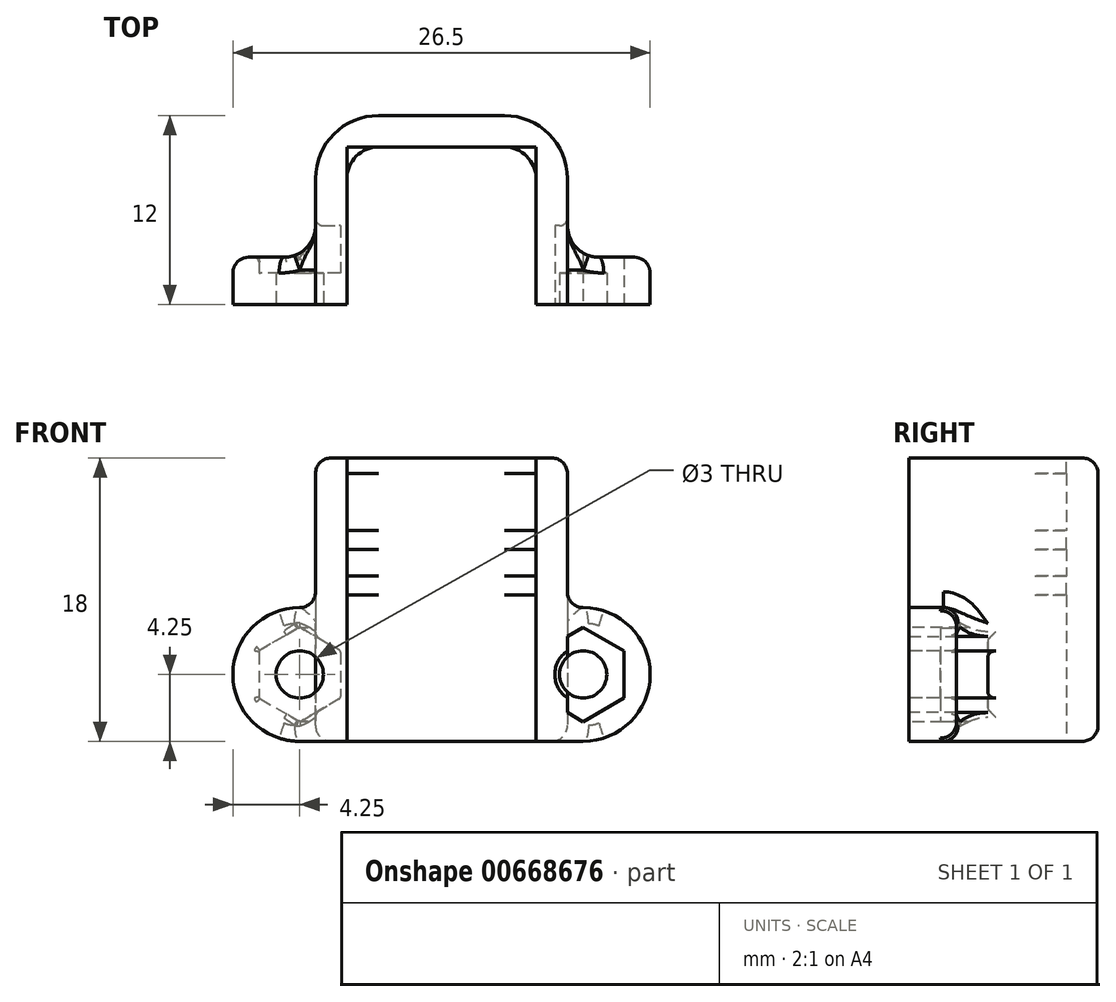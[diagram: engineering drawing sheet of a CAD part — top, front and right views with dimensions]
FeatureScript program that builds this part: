
annotation { "Feature Type Name" : "Feature", "Feature Type Description" : "" }
export const myFeature = defineFeature(function(context is Context, id is Id, definition is map)
    precondition{}
    {
        {
            var Q0;
            Q0=qCreatedBy(makeId("Top.planeOp"),FACE);
            var sketch = newSketch(context, id + "F0", { "sketchPlane" : qUnion([Q0])});
            skLineSegment(sketch, "E0", {"start": v(0, 0) * mm, "end": v(0, 8) * mm});
            skLineSegment(sketch, "E1", {"start": v(2, 10) * mm, "end": v(10, 10) * mm});
            skLineSegment(sketch, "E2", {"start": v(12, 8) * mm, "end": v(12, 0) * mm});
            skLineSegment(sketch, "E3", {"start": v(12, 0) * mm, "end": v(0, 0) * mm, "construction": true});
            skPoint(sketch, "E4.visualSharp", {"position": v(0, 10) * mm});
            skArc(sketch, "E4.filletArc", {"start": v(2, 10) * mm, "mid": v(0.59, 9.41) * mm, "end": v(0, 8) * mm});
            skPoint(sketch, "E5.visualSharp", {"position": v(12, 10) * mm});
            skArc(sketch, "E5.filletArc", {"start": v(12, 8) * mm, "mid": v(11.41, 9.41) * mm, "end": v(10, 10) * mm});
            skLineSegment(sketch, "E6.0", {"start": v(-2, 0) * mm, "end": v(-2, 8) * mm});
            skLineSegment(sketch, "E6.1", {"start": v(14, 8) * mm, "end": v(14, 0) * mm});
            skArc(sketch, "E6.2", {"start": v(14, 8) * mm, "mid": v(12.83, 10.83) * mm, "end": v(10, 12) * mm});
            skLineSegment(sketch, "E6.3", {"start": v(2, 12) * mm, "end": v(10, 12) * mm});
            skArc(sketch, "E6.4", {"start": v(2, 12) * mm, "mid": v(-0.83, 10.83) * mm, "end": v(-2, 8) * mm});
            skLineSegment(sketch, "E7", {"start": v(-2, 0) * mm, "end": v(0, 0) * mm});
            skLineSegment(sketch, "E8", {"start": v(12, 0) * mm, "end": v(14, 0) * mm});
            skSolve(sketch);
        }
        {
            var Q0;
            Q0=qSketchRegion(id+"F0",true);
            extrude(context, id + "F1", {"entities" : qUnion([Q0]), "depth" : 18 * mm});
        }
        {
            var Q0;
            Q0=qCreatedBy(makeId("Front.planeOp"),FACE);
            var sketch = newSketch(context, id + "F2", { "sketchPlane" : qUnion([Q0])});
            skCircle(sketch, "E9", {"center": v(-3, 4.25) * mm, "radius": 1.8 * mm});
            skCircle(sketch, "E10", {"center": v(-3, 4.25) * mm, "radius": 1.5 * mm});
            skLineSegment(sketch, "E11.bottom", {"start": v(1.25, 8.5) * mm, "end": v(-3, 8.5) * mm, "construction": true});
            skLineSegment(sketch, "E11.top", {"start": v(1.25, 0) * mm, "end": v(-3, 0) * mm, "construction": true});
            skLineSegment(sketch, "E11.left", {"start": v(1.25, 8.5) * mm, "end": v(1.25, 0) * mm, "construction": true});
            skLineSegment(sketch, "E11.right", {"start": v(-7.25, 8.5) * mm, "end": v(-7.25, 0) * mm, "construction": true});
            skLineSegment(sketch, "E12", {"start": v(6, 0) * mm, "end": v(6, 18.17) * mm, "construction": true});
            skLineSegment(sketch, "E13", {"start": v(-3, 0) * mm, "end": v(-7.25, 0) * mm, "construction": true});
            skLineSegment(sketch, "E14", {"start": v(-3, 8.5) * mm, "end": v(-7.25, 8.5) * mm, "construction": true});
            skArc(sketch, "E15", {"start": v(-3, 8.5) * mm, "mid": v(-7.25, 4.25) * mm, "end": v(-3, 0) * mm});
            skArc(sketch, "E16", {"start": v(-3, 0) * mm, "mid": v(1.25, 4.25) * mm, "end": v(-3, 8.5) * mm, "construction": true});
            skLineSegment(sketch, "E17", {"start": v(-3, 0) * mm, "end": v(0, 0) * mm});
            skLineSegment(sketch, "E18", {"start": v(0, 0) * mm, "end": v(0, 8.5) * mm});
            skLineSegment(sketch, "E19", {"start": v(0, 8.5) * mm, "end": v(-3, 8.5) * mm});
            skLineSegment(sketch, "E20.MirrorCS", {"start": v(15, 0) * mm, "end": v(12, 0) * mm});
            skLineSegment(sketch, "E21.MirrorCS", {"start": v(12, 8.5) * mm, "end": v(15, 8.5) * mm});
            skCircle(sketch, "E22.MirrorC", {"center": v(15, 4.25) * mm, "radius": 1.5 * mm});
            skCircle(sketch, "E23.MirrorC", {"center": v(15, 4.25) * mm, "radius": 1.8 * mm});
            skLineSegment(sketch, "E24.MirrorCS", {"start": v(10.75, 8.5) * mm, "end": v(10.75, 0) * mm, "construction": true});
            skLineSegment(sketch, "E25.MirrorCS", {"start": v(15, 8.5) * mm, "end": v(19.25, 8.5) * mm, "construction": true});
            skLineSegment(sketch, "E26.MirrorCS", {"start": v(10.75, 0) * mm, "end": v(15, 0) * mm, "construction": true});
            skArc(sketch, "E27.MirrorCS", {"start": v(15, 0) * mm, "mid": v(10.75, 4.25) * mm, "end": v(15, 8.5) * mm, "construction": true});
            skLineSegment(sketch, "E28.MirrorCS", {"start": v(10.75, 8.5) * mm, "end": v(15, 8.5) * mm, "construction": true});
            skLineSegment(sketch, "E29.MirrorCS", {"start": v(19.25, 8.5) * mm, "end": v(19.25, 0) * mm, "construction": true});
            skLineSegment(sketch, "E30.MirrorCS", {"start": v(15, 0) * mm, "end": v(19.25, 0) * mm, "construction": true});
            skLineSegment(sketch, "E31.MirrorCS", {"start": v(12, 0) * mm, "end": v(12, 8.5) * mm});
            skArc(sketch, "E32.MirrorCS", {"start": v(15, 8.5) * mm, "mid": v(19.25, 4.25) * mm, "end": v(15, 0) * mm});
            skCircle(sketch, "E33", {"center": v(15, 4.25) * mm, "radius": 3 * mm, "construction": true});
            skLineSegment(sketch, "E34.0", {"start": v(17.6, 5.75) * mm, "end": v(17.6, 2.75) * mm});
            skLineSegment(sketch, "E34.1", {"start": v(17.6, 2.75) * mm, "end": v(15, 1.25) * mm});
            skLineSegment(sketch, "E34.2", {"start": v(15, 1.25) * mm, "end": v(12.4, 2.75) * mm});
            skLineSegment(sketch, "E34.3", {"start": v(12.4, 2.75) * mm, "end": v(12.4, 5.75) * mm});
            skLineSegment(sketch, "E34.4", {"start": v(12.4, 5.75) * mm, "end": v(15, 7.25) * mm});
            skLineSegment(sketch, "E34.5", {"start": v(15, 7.25) * mm, "end": v(17.6, 5.75) * mm});
            skLineSegment(sketch, "E35.MirrorCS", {"start": v(-5.6, 5.75) * mm, "end": v(-5.6, 2.75) * mm});
            skLineSegment(sketch, "E36.MirrorCS", {"start": v(-3, 7.25) * mm, "end": v(-5.6, 5.75) * mm});
            skLineSegment(sketch, "E37.MirrorCS", {"start": v(-0.4, 5.75) * mm, "end": v(-3, 7.25) * mm});
            skLineSegment(sketch, "E38.MirrorCS", {"start": v(-0.4, 2.75) * mm, "end": v(-0.4, 5.75) * mm});
            skLineSegment(sketch, "E39.MirrorCS", {"start": v(-3, 1.25) * mm, "end": v(-0.4, 2.75) * mm});
            skLineSegment(sketch, "E40.MirrorCS", {"start": v(-5.6, 2.75) * mm, "end": v(-3, 1.25) * mm});
            skSolve(sketch);
        }
        {
            var Q0;
            Q0=makeQuery(id+"F2.imprint","IMPRINT",FACE,{"disambiguationData":[TD([[makeQuery(id+"F2.imprint","IMPRINT",EDGE,{"derivedFrom":sQuery(id+"F2.wireOp",EDGE,"E9")}),-1.0]])]});
            var Q1;
            Q1=makeQuery(id+"F2.imprint","IMPRINT",FACE,{"disambiguationData":[TD([[makeQuery(id+"F2.imprint","IMPRINT",EDGE,{"derivedFrom":sQuery(id+"F2.wireOp",EDGE,"E9")}),1.0]])]});
            var Q2;
            Q2=makeQuery(id+"F2.imprint","IMPRINT",FACE,{"disambiguationData":[TD([[makeQuery(id+"F2.imprint","IMPRINT",EDGE,{"derivedFrom":sQuery(id+"F2.wireOp",EDGE,"E20.MirrorCS")}),-1.0]])]});
            var Q3;
            Q3=makeQuery(id+"F2.imprint","IMPRINT",FACE,{"disambiguationData":[TD([[makeQuery(id+"F2.imprint","IMPRINT",EDGE,{"derivedFrom":sQuery(id+"F2.wireOp",EDGE,"E22.MirrorC")}),1.0]])]});
            var Q4;
            Q4=makeQuery(id+"F2.imprint","IMPRINT",FACE,{"disambiguationData":[TD([[makeQuery(id+"F2.imprint","IMPRINT",EDGE,{"derivedFrom":sQuery(id+"F2.wireOp",EDGE,"E23.MirrorC")}),1.0]])]});
            var Q5;
            Q5=makeQuery(id+"F2.imprint","IMPRINT",FACE,{"disambiguationData":[TD([[makeQuery(id+"F2.imprint","IMPRINT",EDGE,{"derivedFrom":sQuery(id+"F2.wireOp",EDGE,"E15")}),1.0]])]});
            extrude(context, id + "F3", {"entities" : qUnion([Q0, Q1, Q2, Q3, Q4, Q5]), "operationType" : NewBodyOperationType.ADD, "oppositeDirection" : true, "depth" : 3 * mm});
        }
        {
            var Q0;
            Q0=makeQuery(id+"F2.imprint","IMPRINT",FACE,{"disambiguationData":[TD([[makeQuery(id+"F2.imprint","IMPRINT",EDGE,{"derivedFrom":sQuery(id+"F2.wireOp",EDGE,"E10")}),1.0]])]});
            var Q1;
            Q1=makeQuery(id+"F2.imprint","IMPRINT",FACE,{"disambiguationData":[TD([[makeQuery(id+"F2.imprint","IMPRINT",EDGE,{"derivedFrom":sQuery(id+"F2.wireOp",EDGE,"E22.MirrorC")}),-1.0]])]});
            var Q2;
            Q2=sQuery(id+"F2.wireOp",EDGE,"E10");
            extrude(context, id + "F4", {"entities" : qUnion([Q0, Q1]), "operationType" : NewBodyOperationType.REMOVE, "surfaceEntities" : qUnion([Q2]), "oppositeDirection" : true, "depth" : 5 * mm});
        }
        {
            var Q0;
            Q0=makeQuery(id+"F3.boolean.opBoolean","INTERSECT",EDGE,{"derivedFrom":[makeQuery(id+"F1.opExtrude","SWEPT_FACE",FACE,{"disambiguationData":[OSD([sQuery(id+"F0.wireOp",EDGE,"E6.1")])]}),makeQuery(id+"F3.opExtrude","CAP_FACE",FACE,{"disambiguationData":[OSD([sQuery(id+"F2.wireOp",EDGE,"E20.MirrorCS"),sQuery(id+"F2.wireOp",EDGE,"E21.MirrorCS"),sQuery(id+"F2.wireOp",EDGE,"E22.MirrorC"),sQuery(id+"F2.wireOp",EDGE,"E31.MirrorCS"),sQuery(id+"F2.wireOp",EDGE,"E32.MirrorCS")])],"isStart":false})]});
            var Q1;
            Q1=makeQuery(id+"F3.boolean.opBoolean","INTERSECT",EDGE,{"derivedFrom":[makeQuery(id+"F1.opExtrude","SWEPT_FACE",FACE,{"disambiguationData":[OSD([sQuery(id+"F0.wireOp",EDGE,"E6.0")])]}),makeQuery(id+"F3.opExtrude","CAP_FACE",FACE,{"disambiguationData":[OSD([sQuery(id+"F2.wireOp",EDGE,"E10"),sQuery(id+"F2.wireOp",EDGE,"E15"),sQuery(id+"F2.wireOp",EDGE,"E17"),sQuery(id+"F2.wireOp",EDGE,"E18"),sQuery(id+"F2.wireOp",EDGE,"E19")])],"isStart":false})]});
            fillet(context, id + "F5", {"entities" : qUnion([Q0, Q1]), "radius" : 2 * mm, "tangentPropagation" : true, "allowEdgeOverflow" : false});
        }
        {
            var Q0;
            Q0=makeQuery(id+"F3.opExtrude","CAP_EDGE",EDGE,{"disambiguationData":[OSD([sQuery(id+"F2.wireOp",EDGE,"E15")])],"isStart":false});
            var Q1;
            Q1=makeQuery(id+"F3.opExtrude","CAP_EDGE",EDGE,{"disambiguationData":[OSD([sQuery(id+"F2.wireOp",EDGE,"E32.MirrorCS")])],"isStart":false});
            fillet(context, id + "F6", {"entities" : qUnion([Q0, Q1]), "radius" : 1 * mm, "tangentPropagation" : true, "allowEdgeOverflow" : false});
        }
        {
            var Q0;
            Q0=makeQuery(id+"F1.opExtrude","CAP_EDGE",EDGE,{"disambiguationData":[OSD([sQuery(id+"F0.wireOp",EDGE,"E6.3")])],"isStart":false});
            var Q1;
            Q1=makeQuery(id+"F1.opExtrude","CAP_EDGE",EDGE,{"disambiguationData":[OSD([sQuery(id+"F0.wireOp",EDGE,"E6.2")])],"isStart":false});
            var Q2;
            Q2=makeQuery(id+"F1.opExtrude","CAP_EDGE",EDGE,{"disambiguationData":[OSD([sQuery(id+"F0.wireOp",EDGE,"E6.1")])],"isStart":false});
            var Q3;
            Q3=makeQuery(id+"F1.opExtrude","CAP_EDGE",EDGE,{"disambiguationData":[OSD([sQuery(id+"F0.wireOp",EDGE,"E6.4")])],"isStart":false});
            var Q4;
            Q4=makeQuery(id+"F1.opExtrude","CAP_EDGE",EDGE,{"disambiguationData":[OSD([sQuery(id+"F0.wireOp",EDGE,"E6.0")])],"isStart":false});
            fillet(context, id + "F7", {"entities" : qUnion([Q0, Q1, Q2, Q3, Q4]), "radius" : 1 * mm, "tangentPropagation" : true, "allowEdgeOverflow" : false});
        }
        {
            var Q0;
            {var subQ0=makeQuery(id+"F1.opExtrude","SWEPT_FACE",FACE,{"disambiguationData":[OSD([sQuery(id+"F0.wireOp",EDGE,"E6.1")])]});var subQ1=sQuery(id+"F2.wireOp",EDGE,"E21.MirrorCS");Q0=makeQuery(id+"F6.opFillet","BLEND_EDGE",EDGE,{"blendedFrom":[makeQuery(id+"F5.opFillet","BLEND_EDGE",EDGE,{"blendedFrom":[makeQuery(id+"F3.boolean.opBoolean","INTERSECT",EDGE,{"derivedFrom":[subQ0,makeQuery(id+"F3.opExtrude","CAP_FACE",FACE,{"disambiguationData":[OSD([sQuery(id+"F2.wireOp",EDGE,"E20.MirrorCS"),subQ1,sQuery(id+"F2.wireOp",EDGE,"E22.MirrorC"),sQuery(id+"F2.wireOp",EDGE,"E31.MirrorCS"),sQuery(id+"F2.wireOp",EDGE,"E32.MirrorCS")])],"isStart":false})]}),makeQuery(id+"F3.opExtrude","SWEPT_FACE",FACE,{"disambiguationData":[OSD([subQ1])]})],"blendedInto":[makeQuery(id+"F3.opExtrude","SWEPT_FACE",FACE,{"disambiguationData":[OSD([subQ1])]})]}),subQ0],"blendedInto":[subQ0]});}
            var Q1;
            Q1=makeQuery(id+"F3.boolean.opBoolean","INTERSECT",EDGE,{"derivedFrom":[makeQuery(id+"F1.opExtrude","SWEPT_FACE",FACE,{"disambiguationData":[OSD([sQuery(id+"F0.wireOp",EDGE,"E6.1")])]}),makeQuery(id+"F3.opExtrude","SWEPT_FACE",FACE,{"disambiguationData":[OSD([sQuery(id+"F2.wireOp",EDGE,"E21.MirrorCS")])]})]});
            var Q2;
            {var subQ0=makeQuery(id+"F1.opExtrude","SWEPT_FACE",FACE,{"disambiguationData":[OSD([sQuery(id+"F0.wireOp",EDGE,"E6.0")])]});var subQ1=sQuery(id+"F2.wireOp",EDGE,"E19");Q2=makeQuery(id+"F6.opFillet","BLEND_EDGE",EDGE,{"blendedFrom":[makeQuery(id+"F5.opFillet","BLEND_EDGE",EDGE,{"blendedFrom":[makeQuery(id+"F3.boolean.opBoolean","INTERSECT",EDGE,{"derivedFrom":[subQ0,makeQuery(id+"F3.opExtrude","CAP_FACE",FACE,{"disambiguationData":[OSD([sQuery(id+"F2.wireOp",EDGE,"E10"),sQuery(id+"F2.wireOp",EDGE,"E15"),sQuery(id+"F2.wireOp",EDGE,"E17"),sQuery(id+"F2.wireOp",EDGE,"E18"),subQ1])],"isStart":false})]}),makeQuery(id+"F3.opExtrude","SWEPT_FACE",FACE,{"disambiguationData":[OSD([subQ1])]})],"blendedInto":[makeQuery(id+"F3.opExtrude","SWEPT_FACE",FACE,{"disambiguationData":[OSD([subQ1])]})]}),subQ0],"blendedInto":[subQ0]});}
            var Q3;
            Q3=makeQuery(id+"F3.boolean.opBoolean","INTERSECT",EDGE,{"derivedFrom":[makeQuery(id+"F1.opExtrude","SWEPT_FACE",FACE,{"disambiguationData":[OSD([sQuery(id+"F0.wireOp",EDGE,"E6.0")])]}),makeQuery(id+"F3.opExtrude","SWEPT_FACE",FACE,{"disambiguationData":[OSD([sQuery(id+"F2.wireOp",EDGE,"E19")])]})]});
            fillet(context, id + "F8", {"entities" : qUnion([Q0, Q1, Q2, Q3]), "radius" : 1 * mm, "tangentPropagation" : true, "allowEdgeOverflow" : false});
        }
        {
            var Q0;
            Q0=makeQuery(id+"F2.imprint","IMPRINT",FACE,{"disambiguationData":[TD([[makeQuery(id+"F2.imprint","IMPRINT",EDGE,{"derivedFrom":sQuery(id+"F2.wireOp",EDGE,"E23.MirrorC")}),1.0]])]});
            var Q1;
            Q1=makeQuery(id+"F2.imprint","IMPRINT",FACE,{"disambiguationData":[TD([[makeQuery(id+"F2.imprint","IMPRINT",EDGE,{"derivedFrom":sQuery(id+"F2.wireOp",EDGE,"E22.MirrorC")}),1.0]])]});
            var Q2;
            Q2=makeQuery(id+"F2.imprint","IMPRINT",FACE,{"disambiguationData":[TD([[makeQuery(id+"F2.imprint","IMPRINT",EDGE,{"derivedFrom":sQuery(id+"F2.wireOp",EDGE,"E9")}),-1.0]])]});
            var Q3;
            Q3=makeQuery(id+"F2.imprint","IMPRINT",FACE,{"disambiguationData":[TD([[makeQuery(id+"F2.imprint","IMPRINT",EDGE,{"derivedFrom":sQuery(id+"F2.wireOp",EDGE,"E9")}),1.0]])]});
            var Q4;
            Q4=makeQuery(id+"F4.boolean.opBoolean","COPY",FACE,{"derivedFrom":makeQuery(id+"F4.opExtrude","CAP_FACE",FACE,{"disambiguationData":[OSD([sQuery(id+"F2.wireOp",EDGE,"E10")])],"isStart":false})});
            extrude(context, id + "F9", {"entities" : qUnion([Q0, Q1, Q2, Q3]), "operationType" : NewBodyOperationType.REMOVE, "endBound" : BoundingType.UP_TO_SURFACE, "oppositeDirection" : true, "endBoundEntityFace" : qUnion([Q4]), "depth" : 4 * mm, "hasSecondDirection" : true, "secondDirectionOppositeDirection" : true, "secondDirectionDepth" : 2 * mm});
        }
        {
            var Q0;
            Q0=qCreatedBy(makeId("Front.planeOp"),FACE);
            var sketch = newSketch(context, id + "F10", { "sketchPlane" : qUnion([Q0])});
            skLineSegment(sketch, "E41.bottom", {"start": v(0, 0) * mm, "end": v(12, 0) * mm, "construction": true});
            skLineSegment(sketch, "E41.top", {"start": v(0, 18) * mm, "end": v(12, 18) * mm, "construction": true});
            skLineSegment(sketch, "E41.left", {"start": v(0, 0) * mm, "end": v(0, 18) * mm, "construction": true});
            skLineSegment(sketch, "E41.right", {"start": v(12, 0) * mm, "end": v(12, 18) * mm, "construction": true});
            skPoint(sketch, "E42", {"position": v(0, 17.6) * mm});
            skPoint(sketch, "E43", {"position": v(0, 12.8) * mm});
            skPoint(sketch, "E44", {"position": v(0, 9.9) * mm});
            skLineSegment(sketch, "E45.bottom", {"start": v(0, 17) * mm, "end": v(12, 17) * mm});
            skLineSegment(sketch, "E45.top", {"start": v(0, 18.2) * mm, "end": v(12, 18.2) * mm});
            skLineSegment(sketch, "E45.left", {"start": v(0, 17) * mm, "end": v(0, 18.2) * mm});
            skLineSegment(sketch, "E45.right", {"start": v(12, 17) * mm, "end": v(12, 18.2) * mm});
            skLineSegment(sketch, "E46.bottom", {"start": v(0, 12.2) * mm, "end": v(12, 12.2) * mm});
            skLineSegment(sketch, "E46.top", {"start": v(0, 13.4) * mm, "end": v(12, 13.4) * mm});
            skLineSegment(sketch, "E46.left", {"start": v(0, 12.2) * mm, "end": v(0, 13.4) * mm});
            skLineSegment(sketch, "E46.right", {"start": v(12, 12.2) * mm, "end": v(12, 13.4) * mm});
            skLineSegment(sketch, "E47.bottom", {"start": v(0, 9.3) * mm, "end": v(12, 9.3) * mm});
            skLineSegment(sketch, "E47.top", {"start": v(0, 10.5) * mm, "end": v(12, 10.5) * mm});
            skLineSegment(sketch, "E47.left", {"start": v(0, 9.3) * mm, "end": v(0, 10.5) * mm});
            skLineSegment(sketch, "E47.right", {"start": v(12, 9.3) * mm, "end": v(12, 10.5) * mm});
            skSolve(sketch);
        }
        {
            var Q0;
            Q0=qSketchRegion(id+"F10",true);
            var Q1;
            Q1=makeQuery(id+"F1.opExtrude","SWEPT_FACE",FACE,{"disambiguationData":[OSD([sQuery(id+"F0.wireOp",EDGE,"E1")])]});
            extrude(context, id + "F11", {"entities" : qUnion([Q0]), "operationType" : NewBodyOperationType.REMOVE, "endBound" : BoundingType.UP_TO_SURFACE, "oppositeDirection" : true, "endBoundEntityFace" : qUnion([Q1]), "depth" : 25 * mm});
        }
        {
            var Q0;
            {var subQ0=makeQuery(id+"F1.opExtrude","SWEPT_FACE",FACE,{"disambiguationData":[OSD([sQuery(id+"F0.wireOp",EDGE,"E6.0")])]});var subQ1=subQ0;var subQ2=subQ1;var subQ3=sQuery(id+"F2.wireOp",EDGE,"E10");var subQ4=makeQuery(id+"F3.opExtrude","CAP_FACE",FACE,{"disambiguationData":[OSD([subQ3,sQuery(id+"F2.wireOp",EDGE,"E15"),sQuery(id+"F2.wireOp",EDGE,"E17"),sQuery(id+"F2.wireOp",EDGE,"E18"),sQuery(id+"F2.wireOp",EDGE,"E19")])],"isStart":false});Q0=makeQuery(id+"F9.boolean.opBoolean","MERGE",EDGE,{"derivedFrom":[makeQuery(id+"F4.boolean.opBoolean","INTERSECT",EDGE,{"derivedFrom":[subQ1,makeQuery(id+"F4.opExtrude","CAP_FACE",FACE,{"disambiguationData":[OSD([subQ3])],"isStart":false})]}),makeQuery(id+"F5.opFillet","BLEND_EDGE",EDGE,{"blendedFrom":[makeQuery(id+"F3.boolean.opBoolean","INTERSECT",EDGE,{"disambiguationData":[OD(0.0)],"derivedFrom":[subQ0,subQ4]}),subQ2],"blendedInto":[subQ2]}),makeQuery(id+"F5.opFillet","BLEND_EDGE",EDGE,{"blendedFrom":[makeQuery(id+"F3.boolean.opBoolean","INTERSECT",EDGE,{"disambiguationData":[OD(1.0)],"derivedFrom":[subQ0,subQ4]}),subQ2],"blendedInto":[subQ2]})]});}
            var Q1;
            {var subQ0=sQuery(id+"F2.wireOp",EDGE,"E19");var subQ1=sQuery(id+"F2.wireOp",EDGE,"E18");var subQ2=sQuery(id+"F2.wireOp",EDGE,"E17");var subQ3=sQuery(id+"F2.wireOp",EDGE,"E15");var subQ4=sQuery(id+"F2.wireOp",EDGE,"E10");var subQ5=sQuery(id+"F0.wireOp",EDGE,"E6.0");Q1=makeQuery(id+"F9.boolean.opBoolean","INTERSECT",EDGE,{"derivedFrom":[makeQuery(id+"F5.opFillet","BLEND_FACE",FACE,{"disambiguationData":[OSD([subQ5,subQ4,subQ3,subQ2,subQ1,subQ0]),TDD([makeQuery(id+"F3.boolean.opBoolean","INTERSECT",EDGE,{"disambiguationData":[OD(0.0)],"derivedFrom":[makeQuery(id+"F1.opExtrude","SWEPT_FACE",FACE,{"disambiguationData":[OSD([subQ5])]}),makeQuery(id+"F3.opExtrude","CAP_FACE",FACE,{"disambiguationData":[OSD([subQ4,subQ3,subQ2,subQ1,subQ0])],"isStart":false})]})])]}),makeQuery(id+"F9.opExtrude","SWEPT_FACE",FACE,{"disambiguationData":[OSD([sQuery(id+"F2.wireOp",EDGE,"E39.MirrorCS")])]})]});}
            var Q2;
            {var subQ0=sQuery(id+"F2.wireOp",EDGE,"E19");var subQ1=sQuery(id+"F2.wireOp",EDGE,"E18");var subQ2=sQuery(id+"F2.wireOp",EDGE,"E17");var subQ3=sQuery(id+"F2.wireOp",EDGE,"E15");var subQ4=sQuery(id+"F2.wireOp",EDGE,"E10");var subQ5=sQuery(id+"F0.wireOp",EDGE,"E6.0");Q2=makeQuery(id+"F9.boolean.opBoolean","INTERSECT",EDGE,{"derivedFrom":[makeQuery(id+"F5.opFillet","BLEND_FACE",FACE,{"disambiguationData":[OSD([subQ5,subQ4,subQ3,subQ2,subQ1,subQ0]),TDD([makeQuery(id+"F3.boolean.opBoolean","INTERSECT",EDGE,{"disambiguationData":[OD(1.0)],"derivedFrom":[makeQuery(id+"F1.opExtrude","SWEPT_FACE",FACE,{"disambiguationData":[OSD([subQ5])]}),makeQuery(id+"F3.opExtrude","CAP_FACE",FACE,{"disambiguationData":[OSD([subQ4,subQ3,subQ2,subQ1,subQ0])],"isStart":false})]})])]}),makeQuery(id+"F9.opExtrude","SWEPT_FACE",FACE,{"disambiguationData":[OSD([sQuery(id+"F2.wireOp",EDGE,"E37.MirrorCS")])]})]});}
            var Q3;
            {var subQ0=sQuery(id+"F2.wireOp",EDGE,"E32.MirrorCS");var subQ1=sQuery(id+"F2.wireOp",EDGE,"E31.MirrorCS");var subQ2=sQuery(id+"F2.wireOp",EDGE,"E22.MirrorC");var subQ3=sQuery(id+"F2.wireOp",EDGE,"E21.MirrorCS");var subQ4=sQuery(id+"F2.wireOp",EDGE,"E20.MirrorCS");var subQ5=sQuery(id+"F0.wireOp",EDGE,"E6.1");Q3=makeQuery(id+"F9.boolean.opBoolean","INTERSECT",EDGE,{"derivedFrom":[makeQuery(id+"F5.opFillet","BLEND_FACE",FACE,{"disambiguationData":[OSD([subQ5,subQ4,subQ3,subQ2,subQ1,subQ0]),TDD([makeQuery(id+"F3.boolean.opBoolean","INTERSECT",EDGE,{"disambiguationData":[OD(0.0)],"derivedFrom":[makeQuery(id+"F1.opExtrude","SWEPT_FACE",FACE,{"disambiguationData":[OSD([subQ5])]}),makeQuery(id+"F3.opExtrude","CAP_FACE",FACE,{"disambiguationData":[OSD([subQ4,subQ3,subQ2,subQ1,subQ0])],"isStart":false})]})])]}),makeQuery(id+"F9.opExtrude","SWEPT_FACE",FACE,{"disambiguationData":[OSD([sQuery(id+"F2.wireOp",EDGE,"E34.2")])]})]});}
            var Q4;
            {var subQ0=makeQuery(id+"F1.opExtrude","SWEPT_FACE",FACE,{"disambiguationData":[OSD([sQuery(id+"F0.wireOp",EDGE,"E6.1")])]});var subQ1=subQ0;var subQ2=subQ1;var subQ3=sQuery(id+"F2.wireOp",EDGE,"E22.MirrorC");var subQ4=makeQuery(id+"F3.opExtrude","CAP_FACE",FACE,{"disambiguationData":[OSD([sQuery(id+"F2.wireOp",EDGE,"E20.MirrorCS"),sQuery(id+"F2.wireOp",EDGE,"E21.MirrorCS"),subQ3,sQuery(id+"F2.wireOp",EDGE,"E31.MirrorCS"),sQuery(id+"F2.wireOp",EDGE,"E32.MirrorCS")])],"isStart":false});Q4=makeQuery(id+"F9.boolean.opBoolean","MERGE",EDGE,{"derivedFrom":[makeQuery(id+"F4.boolean.opBoolean","INTERSECT",EDGE,{"derivedFrom":[subQ1,makeQuery(id+"F4.opExtrude","CAP_FACE",FACE,{"disambiguationData":[OSD([subQ3])],"isStart":false})]}),makeQuery(id+"F5.opFillet","BLEND_EDGE",EDGE,{"blendedFrom":[makeQuery(id+"F3.boolean.opBoolean","INTERSECT",EDGE,{"disambiguationData":[OD(1.0)],"derivedFrom":[subQ0,subQ4]}),subQ2],"blendedInto":[subQ2]}),makeQuery(id+"F5.opFillet","BLEND_EDGE",EDGE,{"blendedFrom":[makeQuery(id+"F3.boolean.opBoolean","INTERSECT",EDGE,{"disambiguationData":[OD(0.0)],"derivedFrom":[subQ0,subQ4]}),subQ2],"blendedInto":[subQ2]})]});}
            var Q5;
            {var subQ0=sQuery(id+"F2.wireOp",EDGE,"E32.MirrorCS");var subQ1=sQuery(id+"F2.wireOp",EDGE,"E31.MirrorCS");var subQ2=sQuery(id+"F2.wireOp",EDGE,"E22.MirrorC");var subQ3=sQuery(id+"F2.wireOp",EDGE,"E21.MirrorCS");var subQ4=sQuery(id+"F2.wireOp",EDGE,"E20.MirrorCS");var subQ5=sQuery(id+"F0.wireOp",EDGE,"E6.1");Q5=makeQuery(id+"F9.boolean.opBoolean","INTERSECT",EDGE,{"derivedFrom":[makeQuery(id+"F5.opFillet","BLEND_FACE",FACE,{"disambiguationData":[OSD([subQ5,subQ4,subQ3,subQ2,subQ1,subQ0]),TDD([makeQuery(id+"F3.boolean.opBoolean","INTERSECT",EDGE,{"disambiguationData":[OD(1.0)],"derivedFrom":[makeQuery(id+"F1.opExtrude","SWEPT_FACE",FACE,{"disambiguationData":[OSD([subQ5])]}),makeQuery(id+"F3.opExtrude","CAP_FACE",FACE,{"disambiguationData":[OSD([subQ4,subQ3,subQ2,subQ1,subQ0])],"isStart":false})]})])]}),makeQuery(id+"F9.opExtrude","SWEPT_FACE",FACE,{"disambiguationData":[OSD([sQuery(id+"F2.wireOp",EDGE,"E34.4")])]})]});}
            fillet(context, id + "F12", {"entities" : qUnion([Q0, Q1, Q2, Q3, Q4, Q5]), "radius" : 0.5 * mm, "tangentPropagation" : true, "allowEdgeOverflow" : false});
        }
        {
            var Q0;
            Q0=makeQuery(id+"F9.boolean.opBoolean","COPY",EDGE,{"derivedFrom":makeQuery(id+"F9.opExtrude","SWEPT_EDGE",EDGE,{"disambiguationData":[OSD([sQuery(id+"F2.wireOp",EDGE,"E34.2"),sQuery(id+"F2.wireOp",EDGE,"E34.3")])]})});
            var Q1;
            Q1=makeQuery(id+"F9.boolean.opBoolean","COPY",EDGE,{"derivedFrom":makeQuery(id+"F9.opExtrude","SWEPT_EDGE",EDGE,{"disambiguationData":[OSD([sQuery(id+"F2.wireOp",EDGE,"E34.3"),sQuery(id+"F2.wireOp",EDGE,"E34.4")])]})});
            var Q2;
            Q2=makeQuery(id+"F9.boolean.opBoolean","COPY",EDGE,{"derivedFrom":makeQuery(id+"F9.opExtrude","SWEPT_EDGE",EDGE,{"disambiguationData":[OSD([sQuery(id+"F2.wireOp",EDGE,"E38.MirrorCS"),sQuery(id+"F2.wireOp",EDGE,"E39.MirrorCS")])]})});
            var Q3;
            Q3=makeQuery(id+"F9.boolean.opBoolean","COPY",EDGE,{"derivedFrom":makeQuery(id+"F9.opExtrude","SWEPT_EDGE",EDGE,{"disambiguationData":[OSD([sQuery(id+"F2.wireOp",EDGE,"E37.MirrorCS"),sQuery(id+"F2.wireOp",EDGE,"E38.MirrorCS")])]})});
            var Q4;
            {var subQ0=sQuery(id+"F2.wireOp",EDGE,"E19");var subQ1=sQuery(id+"F2.wireOp",EDGE,"E18");var subQ2=sQuery(id+"F2.wireOp",EDGE,"E17");var subQ3=sQuery(id+"F2.wireOp",EDGE,"E15");var subQ4=sQuery(id+"F2.wireOp",EDGE,"E10");var subQ5=sQuery(id+"F0.wireOp",EDGE,"E6.0");Q4=makeQuery(id+"F12.opFillet","BLEND_EDGE",EDGE,{"blendedFrom":[makeQuery(id+"F9.boolean.opBoolean","INTERSECT",EDGE,{"derivedFrom":[makeQuery(id+"F5.opFillet","BLEND_FACE",FACE,{"disambiguationData":[OSD([subQ5,subQ4,subQ3,subQ2,subQ1,subQ0]),TDD([makeQuery(id+"F3.boolean.opBoolean","INTERSECT",EDGE,{"disambiguationData":[OD(0.0)],"derivedFrom":[makeQuery(id+"F1.opExtrude","SWEPT_FACE",FACE,{"disambiguationData":[OSD([subQ5])]}),makeQuery(id+"F3.opExtrude","CAP_FACE",FACE,{"disambiguationData":[OSD([subQ4,subQ3,subQ2,subQ1,subQ0])],"isStart":false})]})])]}),makeQuery(id+"F9.opExtrude","SWEPT_FACE",FACE,{"disambiguationData":[OSD([sQuery(id+"F2.wireOp",EDGE,"E39.MirrorCS")])]})]}),makeQuery(id+"F9.boolean.opBoolean","COPY",FACE,{"derivedFrom":makeQuery(id+"F9.opExtrude","SWEPT_FACE",FACE,{"disambiguationData":[OSD([sQuery(id+"F2.wireOp",EDGE,"E40.MirrorCS")])]})})],"blendedInto":[makeQuery(id+"F9.boolean.opBoolean","COPY",FACE,{"derivedFrom":makeQuery(id+"F9.opExtrude","SWEPT_FACE",FACE,{"disambiguationData":[OSD([sQuery(id+"F2.wireOp",EDGE,"E40.MirrorCS")])]})})]});}
            var Q5;
            {var subQ0=sQuery(id+"F2.wireOp",EDGE,"E19");var subQ1=sQuery(id+"F2.wireOp",EDGE,"E18");var subQ2=sQuery(id+"F2.wireOp",EDGE,"E17");var subQ3=sQuery(id+"F2.wireOp",EDGE,"E15");var subQ4=sQuery(id+"F2.wireOp",EDGE,"E10");var subQ5=sQuery(id+"F0.wireOp",EDGE,"E6.0");Q5=makeQuery(id+"F12.opFillet","BLEND_EDGE",EDGE,{"blendedFrom":[makeQuery(id+"F9.boolean.opBoolean","INTERSECT",EDGE,{"derivedFrom":[makeQuery(id+"F5.opFillet","BLEND_FACE",FACE,{"disambiguationData":[OSD([subQ5,subQ4,subQ3,subQ2,subQ1,subQ0]),TDD([makeQuery(id+"F3.boolean.opBoolean","INTERSECT",EDGE,{"disambiguationData":[OD(1.0)],"derivedFrom":[makeQuery(id+"F1.opExtrude","SWEPT_FACE",FACE,{"disambiguationData":[OSD([subQ5])]}),makeQuery(id+"F3.opExtrude","CAP_FACE",FACE,{"disambiguationData":[OSD([subQ4,subQ3,subQ2,subQ1,subQ0])],"isStart":false})]})])]}),makeQuery(id+"F9.opExtrude","SWEPT_FACE",FACE,{"disambiguationData":[OSD([sQuery(id+"F2.wireOp",EDGE,"E37.MirrorCS")])]})]}),makeQuery(id+"F9.boolean.opBoolean","COPY",FACE,{"derivedFrom":makeQuery(id+"F9.opExtrude","SWEPT_FACE",FACE,{"disambiguationData":[OSD([sQuery(id+"F2.wireOp",EDGE,"E36.MirrorCS")])]})})],"blendedInto":[makeQuery(id+"F9.boolean.opBoolean","COPY",FACE,{"derivedFrom":makeQuery(id+"F9.opExtrude","SWEPT_FACE",FACE,{"disambiguationData":[OSD([sQuery(id+"F2.wireOp",EDGE,"E36.MirrorCS")])]})})]});}
            var Q6;
            {var subQ0=sQuery(id+"F2.wireOp",EDGE,"E32.MirrorCS");var subQ1=sQuery(id+"F2.wireOp",EDGE,"E31.MirrorCS");var subQ2=sQuery(id+"F2.wireOp",EDGE,"E22.MirrorC");var subQ3=sQuery(id+"F2.wireOp",EDGE,"E21.MirrorCS");var subQ4=sQuery(id+"F2.wireOp",EDGE,"E20.MirrorCS");var subQ5=sQuery(id+"F0.wireOp",EDGE,"E6.1");Q6=makeQuery(id+"F12.opFillet","BLEND_EDGE",EDGE,{"blendedFrom":[makeQuery(id+"F9.boolean.opBoolean","INTERSECT",EDGE,{"derivedFrom":[makeQuery(id+"F5.opFillet","BLEND_FACE",FACE,{"disambiguationData":[OSD([subQ5,subQ4,subQ3,subQ2,subQ1,subQ0]),TDD([makeQuery(id+"F3.boolean.opBoolean","INTERSECT",EDGE,{"disambiguationData":[OD(1.0)],"derivedFrom":[makeQuery(id+"F1.opExtrude","SWEPT_FACE",FACE,{"disambiguationData":[OSD([subQ5])]}),makeQuery(id+"F3.opExtrude","CAP_FACE",FACE,{"disambiguationData":[OSD([subQ4,subQ3,subQ2,subQ1,subQ0])],"isStart":false})]})])]}),makeQuery(id+"F9.opExtrude","SWEPT_FACE",FACE,{"disambiguationData":[OSD([sQuery(id+"F2.wireOp",EDGE,"E34.4")])]})]}),makeQuery(id+"F9.boolean.opBoolean","COPY",FACE,{"derivedFrom":makeQuery(id+"F9.opExtrude","SWEPT_FACE",FACE,{"disambiguationData":[OSD([sQuery(id+"F2.wireOp",EDGE,"E34.5")])]})})],"blendedInto":[makeQuery(id+"F9.boolean.opBoolean","COPY",FACE,{"derivedFrom":makeQuery(id+"F9.opExtrude","SWEPT_FACE",FACE,{"disambiguationData":[OSD([sQuery(id+"F2.wireOp",EDGE,"E34.5")])]})})]});}
            var Q7;
            {var subQ0=sQuery(id+"F2.wireOp",EDGE,"E32.MirrorCS");var subQ1=sQuery(id+"F2.wireOp",EDGE,"E31.MirrorCS");var subQ2=sQuery(id+"F2.wireOp",EDGE,"E22.MirrorC");var subQ3=sQuery(id+"F2.wireOp",EDGE,"E21.MirrorCS");var subQ4=sQuery(id+"F2.wireOp",EDGE,"E20.MirrorCS");var subQ5=sQuery(id+"F0.wireOp",EDGE,"E6.1");Q7=makeQuery(id+"F12.opFillet","BLEND_EDGE",EDGE,{"blendedFrom":[makeQuery(id+"F9.boolean.opBoolean","INTERSECT",EDGE,{"derivedFrom":[makeQuery(id+"F5.opFillet","BLEND_FACE",FACE,{"disambiguationData":[OSD([subQ5,subQ4,subQ3,subQ2,subQ1,subQ0]),TDD([makeQuery(id+"F3.boolean.opBoolean","INTERSECT",EDGE,{"disambiguationData":[OD(0.0)],"derivedFrom":[makeQuery(id+"F1.opExtrude","SWEPT_FACE",FACE,{"disambiguationData":[OSD([subQ5])]}),makeQuery(id+"F3.opExtrude","CAP_FACE",FACE,{"disambiguationData":[OSD([subQ4,subQ3,subQ2,subQ1,subQ0])],"isStart":false})]})])]}),makeQuery(id+"F9.opExtrude","SWEPT_FACE",FACE,{"disambiguationData":[OSD([sQuery(id+"F2.wireOp",EDGE,"E34.2")])]})]}),makeQuery(id+"F9.boolean.opBoolean","COPY",FACE,{"derivedFrom":makeQuery(id+"F9.opExtrude","SWEPT_FACE",FACE,{"disambiguationData":[OSD([sQuery(id+"F2.wireOp",EDGE,"E34.1")])]})})],"blendedInto":[makeQuery(id+"F9.boolean.opBoolean","COPY",FACE,{"derivedFrom":makeQuery(id+"F9.opExtrude","SWEPT_FACE",FACE,{"disambiguationData":[OSD([sQuery(id+"F2.wireOp",EDGE,"E34.1")])]})})]});}
            var Q8;
            Q8=makeQuery(id+"F9.boolean.opBoolean","COPY",EDGE,{"derivedFrom":makeQuery(id+"F9.opExtrude","SWEPT_EDGE",EDGE,{"disambiguationData":[OSD([sQuery(id+"F2.wireOp",EDGE,"E34.0"),sQuery(id+"F2.wireOp",EDGE,"E34.1")])]})});
            var Q9;
            Q9=makeQuery(id+"F9.boolean.opBoolean","COPY",EDGE,{"derivedFrom":makeQuery(id+"F9.opExtrude","SWEPT_EDGE",EDGE,{"disambiguationData":[OSD([sQuery(id+"F2.wireOp",EDGE,"E34.0"),sQuery(id+"F2.wireOp",EDGE,"E34.5")])]})});
            var Q10;
            Q10=makeQuery(id+"F9.boolean.opBoolean","COPY",EDGE,{"derivedFrom":makeQuery(id+"F9.opExtrude","SWEPT_EDGE",EDGE,{"disambiguationData":[OSD([sQuery(id+"F2.wireOp",EDGE,"E35.MirrorCS"),sQuery(id+"F2.wireOp",EDGE,"E36.MirrorCS")])]})});
            var Q11;
            Q11=makeQuery(id+"F9.boolean.opBoolean","COPY",EDGE,{"derivedFrom":makeQuery(id+"F9.opExtrude","SWEPT_EDGE",EDGE,{"disambiguationData":[OSD([sQuery(id+"F2.wireOp",EDGE,"E35.MirrorCS"),sQuery(id+"F2.wireOp",EDGE,"E40.MirrorCS")])]})});
            fillet(context, id + "F13", {"entities" : qUnion([Q0, Q1, Q2, Q3, Q4, Q5, Q6, Q7, Q8, Q9, Q10, Q11]), "radius" : 0.2 * mm, "tangentPropagation" : true, "allowEdgeOverflow" : false});
        }
        {
            var Q0;
            Q0=makeQuery(id+"F9.boolean.opBoolean","INTERSECT",EDGE,{"derivedFrom":[makeQuery(id+"F1.opExtrude","SWEPT_FACE",FACE,{"disambiguationData":[OSD([sQuery(id+"F0.wireOp",EDGE,"E6.4")])]}),makeQuery(id+"F9.opExtrude","SWEPT_FACE",FACE,{"disambiguationData":[OSD([sQuery(id+"F2.wireOp",EDGE,"E39.MirrorCS")])]})]});
            var Q1;
            Q1=makeQuery(id+"F9.boolean.opBoolean","INTERSECT",EDGE,{"derivedFrom":[makeQuery(id+"F1.opExtrude","SWEPT_FACE",FACE,{"disambiguationData":[OSD([sQuery(id+"F0.wireOp",EDGE,"E6.4")])]}),makeQuery(id+"F9.opExtrude","SWEPT_FACE",FACE,{"disambiguationData":[OSD([sQuery(id+"F2.wireOp",EDGE,"E38.MirrorCS")])]})]});
            var Q2;
            Q2=makeQuery(id+"F9.boolean.opBoolean","INTERSECT",EDGE,{"derivedFrom":[makeQuery(id+"F1.opExtrude","SWEPT_FACE",FACE,{"disambiguationData":[OSD([sQuery(id+"F0.wireOp",EDGE,"E6.4")])]}),makeQuery(id+"F9.opExtrude","SWEPT_FACE",FACE,{"disambiguationData":[OSD([sQuery(id+"F2.wireOp",EDGE,"E37.MirrorCS")])]})]});
            var Q3;
            {var subQ0=sQuery(id+"F2.wireOp",EDGE,"E19");var subQ1=sQuery(id+"F2.wireOp",EDGE,"E18");var subQ2=sQuery(id+"F2.wireOp",EDGE,"E17");var subQ3=sQuery(id+"F2.wireOp",EDGE,"E15");var subQ4=sQuery(id+"F2.wireOp",EDGE,"E10");var subQ5=sQuery(id+"F0.wireOp",EDGE,"E6.0");Q3=makeQuery(id+"F9.boolean.opBoolean","INTERSECT",EDGE,{"derivedFrom":[makeQuery(id+"F5.opFillet","BLEND_FACE",FACE,{"disambiguationData":[OSD([subQ5,subQ4,subQ3,subQ2,subQ1,subQ0]),TDD([makeQuery(id+"F3.boolean.opBoolean","INTERSECT",EDGE,{"disambiguationData":[OD(0.0)],"derivedFrom":[makeQuery(id+"F1.opExtrude","SWEPT_FACE",FACE,{"disambiguationData":[OSD([subQ5])]}),makeQuery(id+"F3.opExtrude","CAP_FACE",FACE,{"disambiguationData":[OSD([subQ4,subQ3,subQ2,subQ1,subQ0])],"isStart":false})]})])]}),makeQuery(id+"F9.opExtrude","SWEPT_FACE",FACE,{"disambiguationData":[OSD([sQuery(id+"F2.wireOp",EDGE,"E40.MirrorCS")])]})]});}
            var Q4;
            Q4=makeQuery(id+"F9.boolean.opBoolean","INTERSECT",EDGE,{"derivedFrom":[makeQuery(id+"F3.opExtrude","CAP_FACE",FACE,{"disambiguationData":[OSD([sQuery(id+"F2.wireOp",EDGE,"E10"),sQuery(id+"F2.wireOp",EDGE,"E15"),sQuery(id+"F2.wireOp",EDGE,"E17"),sQuery(id+"F2.wireOp",EDGE,"E18"),sQuery(id+"F2.wireOp",EDGE,"E19")])],"isStart":false}),makeQuery(id+"F9.opExtrude","SWEPT_FACE",FACE,{"disambiguationData":[OSD([sQuery(id+"F2.wireOp",EDGE,"E35.MirrorCS")])]})]});
            var Q5;
            Q5=makeQuery(id+"F9.boolean.opBoolean","INTERSECT",EDGE,{"derivedFrom":[makeQuery(id+"F3.opExtrude","CAP_FACE",FACE,{"disambiguationData":[OSD([sQuery(id+"F2.wireOp",EDGE,"E10"),sQuery(id+"F2.wireOp",EDGE,"E15"),sQuery(id+"F2.wireOp",EDGE,"E17"),sQuery(id+"F2.wireOp",EDGE,"E18"),sQuery(id+"F2.wireOp",EDGE,"E19")])],"isStart":false}),makeQuery(id+"F9.opExtrude","SWEPT_FACE",FACE,{"disambiguationData":[OSD([sQuery(id+"F2.wireOp",EDGE,"E36.MirrorCS")])]})]});
            var Q6;
            {var subQ0=sQuery(id+"F2.wireOp",EDGE,"E19");var subQ1=sQuery(id+"F2.wireOp",EDGE,"E18");var subQ2=sQuery(id+"F2.wireOp",EDGE,"E17");var subQ3=sQuery(id+"F2.wireOp",EDGE,"E15");var subQ4=sQuery(id+"F2.wireOp",EDGE,"E10");var subQ5=sQuery(id+"F0.wireOp",EDGE,"E6.0");Q6=makeQuery(id+"F9.boolean.opBoolean","INTERSECT",EDGE,{"derivedFrom":[makeQuery(id+"F5.opFillet","BLEND_FACE",FACE,{"disambiguationData":[OSD([subQ5,subQ4,subQ3,subQ2,subQ1,subQ0]),TDD([makeQuery(id+"F3.boolean.opBoolean","INTERSECT",EDGE,{"disambiguationData":[OD(1.0)],"derivedFrom":[makeQuery(id+"F1.opExtrude","SWEPT_FACE",FACE,{"disambiguationData":[OSD([subQ5])]}),makeQuery(id+"F3.opExtrude","CAP_FACE",FACE,{"disambiguationData":[OSD([subQ4,subQ3,subQ2,subQ1,subQ0])],"isStart":false})]})])]}),makeQuery(id+"F9.opExtrude","SWEPT_FACE",FACE,{"disambiguationData":[OSD([sQuery(id+"F2.wireOp",EDGE,"E36.MirrorCS")])]})]});}
            var Q7;
            Q7=makeQuery(id+"F9.boolean.opBoolean","INTERSECT",EDGE,{"derivedFrom":[makeQuery(id+"F3.opExtrude","CAP_FACE",FACE,{"disambiguationData":[OSD([sQuery(id+"F2.wireOp",EDGE,"E10"),sQuery(id+"F2.wireOp",EDGE,"E15"),sQuery(id+"F2.wireOp",EDGE,"E17"),sQuery(id+"F2.wireOp",EDGE,"E18"),sQuery(id+"F2.wireOp",EDGE,"E19")])],"isStart":false}),makeQuery(id+"F9.opExtrude","SWEPT_FACE",FACE,{"disambiguationData":[OSD([sQuery(id+"F2.wireOp",EDGE,"E40.MirrorCS")])]})]});
            var Q8;
            {var subQ0=sQuery(id+"F2.wireOp",EDGE,"E19");var subQ1=sQuery(id+"F2.wireOp",EDGE,"E18");var subQ2=sQuery(id+"F2.wireOp",EDGE,"E17");var subQ3=sQuery(id+"F2.wireOp",EDGE,"E15");var subQ4=sQuery(id+"F2.wireOp",EDGE,"E10");var subQ5=sQuery(id+"F0.wireOp",EDGE,"E6.0");Q8=makeQuery(id+"F9.boolean.opBoolean","INTERSECT",EDGE,{"derivedFrom":[makeQuery(id+"F5.opFillet","BLEND_FACE",FACE,{"disambiguationData":[OSD([subQ5,subQ4,subQ3,subQ2,subQ1,subQ0]),TDD([makeQuery(id+"F3.boolean.opBoolean","INTERSECT",EDGE,{"disambiguationData":[OD(1.0)],"derivedFrom":[makeQuery(id+"F1.opExtrude","SWEPT_FACE",FACE,{"disambiguationData":[OSD([subQ5])]}),makeQuery(id+"F3.opExtrude","CAP_FACE",FACE,{"disambiguationData":[OSD([subQ4,subQ3,subQ2,subQ1,subQ0])],"isStart":false})]})])]}),makeQuery(id+"F9.opExtrude","SWEPT_FACE",FACE,{"disambiguationData":[OSD([sQuery(id+"F2.wireOp",EDGE,"E37.MirrorCS")])]})]});}
            var Q9;
            Q9=makeQuery(id+"F9.boolean.opBoolean","INTERSECT",EDGE,{"derivedFrom":[makeQuery(id+"F1.opExtrude","SWEPT_FACE",FACE,{"disambiguationData":[OSD([sQuery(id+"F0.wireOp",EDGE,"E6.0")])]}),makeQuery(id+"F9.opExtrude","SWEPT_FACE",FACE,{"disambiguationData":[OSD([sQuery(id+"F2.wireOp",EDGE,"E37.MirrorCS")])]})]});
            var Q10;
            {var subQ0=sQuery(id+"F2.wireOp",EDGE,"E19");var subQ1=sQuery(id+"F2.wireOp",EDGE,"E18");var subQ2=sQuery(id+"F2.wireOp",EDGE,"E17");var subQ3=sQuery(id+"F2.wireOp",EDGE,"E15");var subQ4=sQuery(id+"F2.wireOp",EDGE,"E10");var subQ5=sQuery(id+"F0.wireOp",EDGE,"E6.0");Q10=makeQuery(id+"F9.boolean.opBoolean","INTERSECT",EDGE,{"derivedFrom":[makeQuery(id+"F5.opFillet","BLEND_FACE",FACE,{"disambiguationData":[OSD([subQ5,subQ4,subQ3,subQ2,subQ1,subQ0]),TDD([makeQuery(id+"F3.boolean.opBoolean","INTERSECT",EDGE,{"disambiguationData":[OD(0.0)],"derivedFrom":[makeQuery(id+"F1.opExtrude","SWEPT_FACE",FACE,{"disambiguationData":[OSD([subQ5])]}),makeQuery(id+"F3.opExtrude","CAP_FACE",FACE,{"disambiguationData":[OSD([subQ4,subQ3,subQ2,subQ1,subQ0])],"isStart":false})]})])]}),makeQuery(id+"F9.opExtrude","SWEPT_FACE",FACE,{"disambiguationData":[OSD([sQuery(id+"F2.wireOp",EDGE,"E39.MirrorCS")])]})]});}
            var Q11;
            Q11=makeQuery(id+"F9.boolean.opBoolean","INTERSECT",EDGE,{"derivedFrom":[makeQuery(id+"F1.opExtrude","SWEPT_FACE",FACE,{"disambiguationData":[OSD([sQuery(id+"F0.wireOp",EDGE,"E6.0")])]}),makeQuery(id+"F9.opExtrude","SWEPT_FACE",FACE,{"disambiguationData":[OSD([sQuery(id+"F2.wireOp",EDGE,"E39.MirrorCS")])]})]});
            var Q12;
            Q12=makeQuery(id+"F9.boolean.opBoolean","COPY",EDGE,{"derivedFrom":makeQuery(id+"F9.opExtrude","SWEPT_EDGE",EDGE,{"disambiguationData":[OSD([sQuery(id+"F2.wireOp",EDGE,"E37.MirrorCS"),sQuery(id+"F2.wireOp",EDGE,"E38.MirrorCS")])]})});
            var Q13;
            Q13=makeQuery(id+"F9.boolean.opBoolean","COPY",EDGE,{"derivedFrom":makeQuery(id+"F9.opExtrude","SWEPT_EDGE",EDGE,{"disambiguationData":[OSD([sQuery(id+"F2.wireOp",EDGE,"E38.MirrorCS"),sQuery(id+"F2.wireOp",EDGE,"E39.MirrorCS")])]})});
            var Q14;
            {var subQ0=sQuery(id+"F2.wireOp",EDGE,"E32.MirrorCS");var subQ1=sQuery(id+"F2.wireOp",EDGE,"E31.MirrorCS");var subQ2=sQuery(id+"F2.wireOp",EDGE,"E22.MirrorC");var subQ3=sQuery(id+"F2.wireOp",EDGE,"E21.MirrorCS");var subQ4=sQuery(id+"F2.wireOp",EDGE,"E20.MirrorCS");var subQ5=sQuery(id+"F0.wireOp",EDGE,"E6.1");Q14=makeQuery(id+"F9.boolean.opBoolean","INTERSECT",EDGE,{"derivedFrom":[makeQuery(id+"F5.opFillet","BLEND_FACE",FACE,{"disambiguationData":[OSD([subQ5,subQ4,subQ3,subQ2,subQ1,subQ0]),TDD([makeQuery(id+"F3.boolean.opBoolean","INTERSECT",EDGE,{"disambiguationData":[OD(0.0)],"derivedFrom":[makeQuery(id+"F1.opExtrude","SWEPT_FACE",FACE,{"disambiguationData":[OSD([subQ5])]}),makeQuery(id+"F3.opExtrude","CAP_FACE",FACE,{"disambiguationData":[OSD([subQ4,subQ3,subQ2,subQ1,subQ0])],"isStart":false})]})])]}),makeQuery(id+"F9.opExtrude","SWEPT_FACE",FACE,{"disambiguationData":[OSD([sQuery(id+"F2.wireOp",EDGE,"E34.2")])]})]});}
            var Q15;
            Q15=makeQuery(id+"F9.boolean.opBoolean","INTERSECT",EDGE,{"derivedFrom":[makeQuery(id+"F1.opExtrude","SWEPT_FACE",FACE,{"disambiguationData":[OSD([sQuery(id+"F0.wireOp",EDGE,"E6.1")])]}),makeQuery(id+"F9.opExtrude","SWEPT_FACE",FACE,{"disambiguationData":[OSD([sQuery(id+"F2.wireOp",EDGE,"E34.2")])]})]});
            var Q16;
            Q16=makeQuery(id+"F9.boolean.opBoolean","INTERSECT",EDGE,{"derivedFrom":[makeQuery(id+"F1.opExtrude","SWEPT_FACE",FACE,{"disambiguationData":[OSD([sQuery(id+"F0.wireOp",EDGE,"E6.2")])]}),makeQuery(id+"F9.opExtrude","SWEPT_FACE",FACE,{"disambiguationData":[OSD([sQuery(id+"F2.wireOp",EDGE,"E34.3")])]})]});
            var Q17;
            {var subQ0=sQuery(id+"F2.wireOp",EDGE,"E32.MirrorCS");var subQ1=sQuery(id+"F2.wireOp",EDGE,"E31.MirrorCS");var subQ2=sQuery(id+"F2.wireOp",EDGE,"E22.MirrorC");var subQ3=sQuery(id+"F2.wireOp",EDGE,"E21.MirrorCS");var subQ4=sQuery(id+"F2.wireOp",EDGE,"E20.MirrorCS");var subQ5=sQuery(id+"F0.wireOp",EDGE,"E6.1");Q17=makeQuery(id+"F9.boolean.opBoolean","INTERSECT",EDGE,{"derivedFrom":[makeQuery(id+"F5.opFillet","BLEND_FACE",FACE,{"disambiguationData":[OSD([subQ5,subQ4,subQ3,subQ2,subQ1,subQ0]),TDD([makeQuery(id+"F3.boolean.opBoolean","INTERSECT",EDGE,{"disambiguationData":[OD(1.0)],"derivedFrom":[makeQuery(id+"F1.opExtrude","SWEPT_FACE",FACE,{"disambiguationData":[OSD([subQ5])]}),makeQuery(id+"F3.opExtrude","CAP_FACE",FACE,{"disambiguationData":[OSD([subQ4,subQ3,subQ2,subQ1,subQ0])],"isStart":false})]})])]}),makeQuery(id+"F9.opExtrude","SWEPT_FACE",FACE,{"disambiguationData":[OSD([sQuery(id+"F2.wireOp",EDGE,"E34.4")])]})]});}
            var Q18;
            Q18=makeQuery(id+"F9.boolean.opBoolean","INTERSECT",EDGE,{"derivedFrom":[makeQuery(id+"F3.opExtrude","CAP_FACE",FACE,{"disambiguationData":[OSD([sQuery(id+"F2.wireOp",EDGE,"E20.MirrorCS"),sQuery(id+"F2.wireOp",EDGE,"E21.MirrorCS"),sQuery(id+"F2.wireOp",EDGE,"E22.MirrorC"),sQuery(id+"F2.wireOp",EDGE,"E31.MirrorCS"),sQuery(id+"F2.wireOp",EDGE,"E32.MirrorCS")])],"isStart":false}),makeQuery(id+"F9.opExtrude","SWEPT_FACE",FACE,{"disambiguationData":[OSD([sQuery(id+"F2.wireOp",EDGE,"E34.5")])]})]});
            var Q19;
            Q19=makeQuery(id+"F9.boolean.opBoolean","INTERSECT",EDGE,{"derivedFrom":[makeQuery(id+"F3.opExtrude","CAP_FACE",FACE,{"disambiguationData":[OSD([sQuery(id+"F2.wireOp",EDGE,"E20.MirrorCS"),sQuery(id+"F2.wireOp",EDGE,"E21.MirrorCS"),sQuery(id+"F2.wireOp",EDGE,"E22.MirrorC"),sQuery(id+"F2.wireOp",EDGE,"E31.MirrorCS"),sQuery(id+"F2.wireOp",EDGE,"E32.MirrorCS")])],"isStart":false}),makeQuery(id+"F9.opExtrude","SWEPT_FACE",FACE,{"disambiguationData":[OSD([sQuery(id+"F2.wireOp",EDGE,"E34.0")])]})]});
            var Q20;
            Q20=makeQuery(id+"F9.boolean.opBoolean","INTERSECT",EDGE,{"derivedFrom":[makeQuery(id+"F3.opExtrude","CAP_FACE",FACE,{"disambiguationData":[OSD([sQuery(id+"F2.wireOp",EDGE,"E20.MirrorCS"),sQuery(id+"F2.wireOp",EDGE,"E21.MirrorCS"),sQuery(id+"F2.wireOp",EDGE,"E22.MirrorC"),sQuery(id+"F2.wireOp",EDGE,"E31.MirrorCS"),sQuery(id+"F2.wireOp",EDGE,"E32.MirrorCS")])],"isStart":false}),makeQuery(id+"F9.opExtrude","SWEPT_FACE",FACE,{"disambiguationData":[OSD([sQuery(id+"F2.wireOp",EDGE,"E34.1")])]})]});
            var Q21;
            Q21=makeQuery(id+"F9.boolean.opBoolean","COPY",EDGE,{"derivedFrom":makeQuery(id+"F9.opExtrude","SWEPT_EDGE",EDGE,{"disambiguationData":[OSD([sQuery(id+"F2.wireOp",EDGE,"E34.3"),sQuery(id+"F2.wireOp",EDGE,"E34.4")])]})});
            var Q22;
            Q22=makeQuery(id+"F9.boolean.opBoolean","COPY",EDGE,{"derivedFrom":makeQuery(id+"F9.opExtrude","SWEPT_EDGE",EDGE,{"disambiguationData":[OSD([sQuery(id+"F2.wireOp",EDGE,"E34.2"),sQuery(id+"F2.wireOp",EDGE,"E34.3")])]})});
            fillet(context, id + "F14", {"entities" : qUnion([Q0, Q1, Q2, Q3, Q4, Q5, Q6, Q7, Q8, Q9, Q10, Q11, Q12, Q13, Q14, Q15, Q16, Q17, Q18, Q19, Q20, Q21, Q22]), "radius" : 0.3 * mm, "tangentPropagation" : true, "allowEdgeOverflow" : false});
        }
    });
